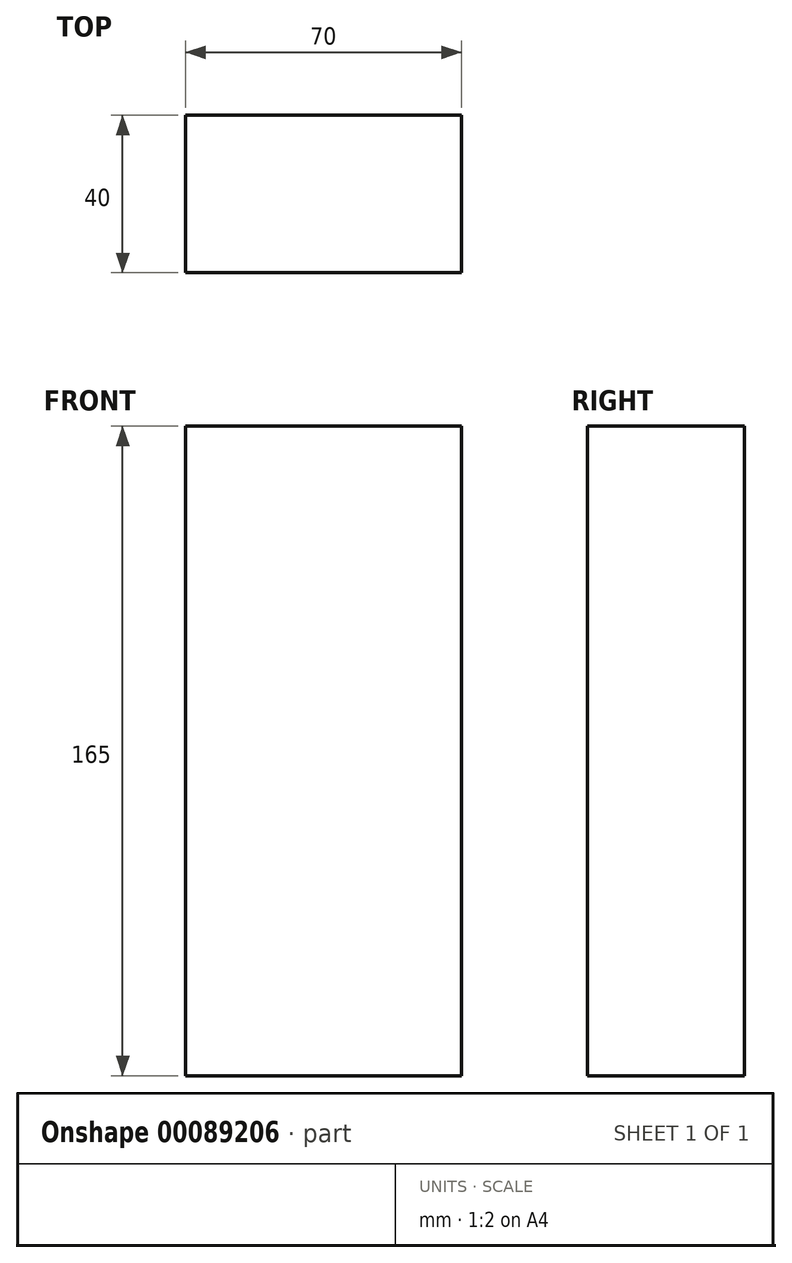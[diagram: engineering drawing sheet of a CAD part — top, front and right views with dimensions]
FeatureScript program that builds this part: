
annotation { "Feature Type Name" : "Feature", "Feature Type Description" : "" }
export const myFeature = defineFeature(function(context is Context, id is Id, definition is map)
    precondition{}
    {
        {
            var Q0;
            Q0=qCreatedBy(makeId("Front.planeOp"),FACE);
            var sketch = newSketch(context, id + "F0", { "sketchPlane" : qUnion([Q0])});
            skLineSegment(sketch, "E0.bottom", {"start": v(-224.9, -66.23) * mm, "end": v(-154.9, -66.23) * mm});
            skLineSegment(sketch, "E0.top", {"start": v(-224.9, 98.77) * mm, "end": v(-154.9, 98.77) * mm});
            skLineSegment(sketch, "E0.left", {"start": v(-224.9, -66.23) * mm, "end": v(-224.9, 98.77) * mm});
            skLineSegment(sketch, "E0.right", {"start": v(-154.9, -66.23) * mm, "end": v(-154.9, 98.77) * mm});
            skSolve(sketch);
        }
        {
            var Q0;
            Q0=makeQuery(id+"F0.imprint","IMPRINT",FACE,{"disambiguationData":[TD([[makeQuery(id+"F0.imprint","IMPRINT",EDGE,{"derivedFrom":sQuery(id+"F0.wireOp",EDGE,"E0.bottom")}),1.0]])]});
            extrude(context, id + "F1", {"entities" : qUnion([Q0]), "depth" : 40 * mm});
        }
    });
